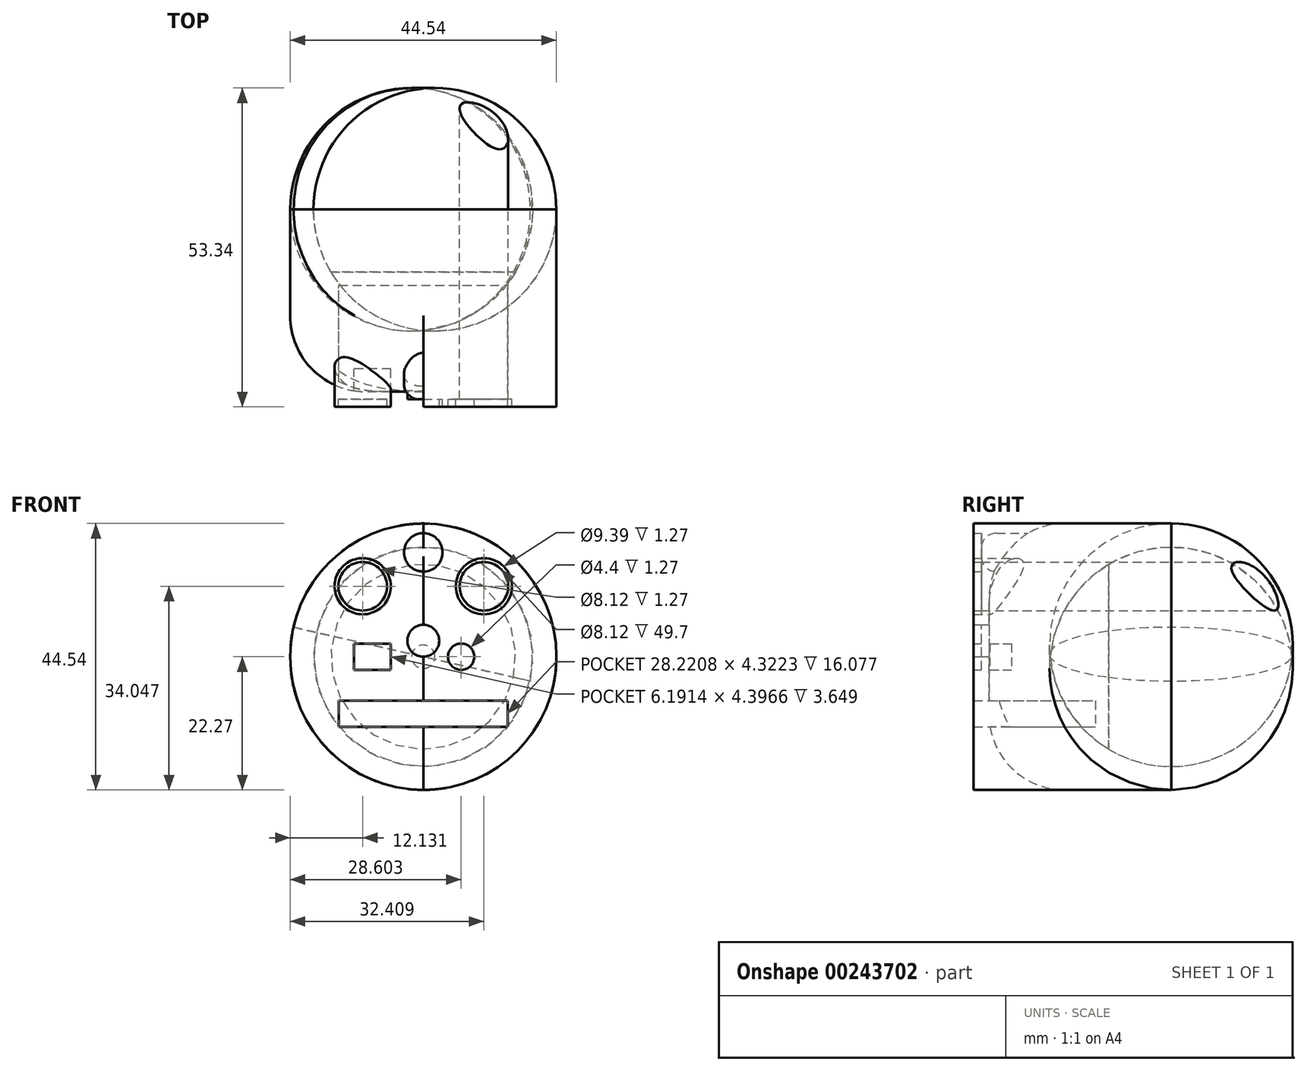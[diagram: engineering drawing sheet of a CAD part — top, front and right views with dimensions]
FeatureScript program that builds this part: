
annotation { "Feature Type Name" : "Feature", "Feature Type Description" : "" }
export const myFeature = defineFeature(function(context is Context, id is Id, definition is map)
    precondition{}
    {
        {
            var Q0;
            Q0=qCreatedBy(makeId("Front.planeOp"),FACE);
            var sketch = newSketch(context, id + "F0", { "sketchPlane" : qUnion([Q0])});
            skCircle(sketch, "E0", {"center": v(0, 0) * mm, "radius": 22.27 * mm});
            skLineSegment(sketch, "E1", {"start": v(0, 22.27) * mm, "end": v(0, -22.27) * mm});
            skCircle(sketch, "E2", {"center": v(-10.14, 11.78) * mm, "radius": 4.7 * mm});
            skLineSegment(sketch, "E3.bottom", {"start": v(-14.11, -7.38) * mm, "end": v(14.11, -7.38) * mm});
            skLineSegment(sketch, "E3.top", {"start": v(-14.11, -11.7) * mm, "end": v(14.11, -11.7) * mm});
            skLineSegment(sketch, "E3.left", {"start": v(-14.11, -7.38) * mm, "end": v(-14.11, -11.7) * mm});
            skLineSegment(sketch, "E3.right", {"start": v(14.11, -7.38) * mm, "end": v(14.11, -11.7) * mm});
            skPoint(sketch, "E3.middle", {"position": v(0, -9.54) * mm});
            skCircle(sketch, "E4", {"center": v(0, 2.67) * mm, "radius": 2.67 * mm});
            skCircle(sketch, "E5", {"center": v(0, 17.44) * mm, "radius": 3.22 * mm});
            skCircle(sketch, "E6.MirrorC", {"center": v(10.14, 11.78) * mm, "radius": 4.7 * mm});
            skLineSegment(sketch, "E7.bottom", {"start": v(-5.4, 2.2) * mm, "end": v(-11.6, 2.2) * mm});
            skLineSegment(sketch, "E7.top", {"start": v(-5.4, -2.2) * mm, "end": v(-11.6, -2.2) * mm});
            skLineSegment(sketch, "E7.left", {"start": v(-5.4, 2.2) * mm, "end": v(-5.4, -2.2) * mm});
            skLineSegment(sketch, "E7.right", {"start": v(-11.6, 2.2) * mm, "end": v(-11.6, -2.2) * mm});
            skPoint(sketch, "E7.middle", {"position": v(-8.5, 0) * mm});
            skCircle(sketch, "E8", {"center": v(6.33, 0) * mm, "radius": 2.2 * mm});
            skCircle(sketch, "E9", {"center": v(-10.14, 11.78) * mm, "radius": 4.06 * mm});
            skCircle(sketch, "E10.MirrorC", {"center": v(10.14, 11.78) * mm, "radius": 4.06 * mm});
            skSolve(sketch);
        }
        {
            var Q0;
            Q0=makeQuery(id+"F0.imprint","IMPRINT",FACE,{"disambiguationData":[TD([[makeQuery(id+"F0.imprint","IMPRINT",EDGE,{"derivedFrom":sQuery(id+"F0.wireOp",EDGE,"E2")}),-1.0]])]});
            var Q1;
            {var subQ4=sQuery(id+"F0.wireOp",EDGE,"E3.right");Q1=makeQuery(id+"F0.imprint","IMPRINT",FACE,{"disambiguationData":[TD([[makeQuery(id+"F0.imprint","IMPRINT",EDGE,{"derivedFrom":subQ4}),1.0]])]});}
            extrude(context, id + "F1", {"entities" : qUnion([Q0, Q1]), "depth" : 38.1 * mm});
        }
        {
            var Q0;
            Q0=makeQuery(id+"F1.opExtrude","CAP_EDGE",EDGE,{"disambiguationData":[OSD([sQuery(id+"F0.wireOp",EDGE,"E0")])],"isStart":false});
            fillet(context, id + "F2", {"entities" : qUnion([Q0]), "radius" : 12.7 * mm, "tangentPropagation" : true, "allowEdgeOverflow" : false});
        }
        {
            var Q0;
            Q0=makeQuery(id+"F0.imprint","IMPRINT",FACE,{"disambiguationData":[TD([[makeQuery(id+"F0.imprint","IMPRINT",EDGE,{"derivedFrom":sQuery(id+"F0.wireOp",EDGE,"E2")}),1.0]])]});
            var Q1;
            Q1=makeQuery(id+"F0.imprint","IMPRINT",FACE,{"disambiguationData":[TD([[makeQuery(id+"F0.imprint","IMPRINT",EDGE,{"derivedFrom":sQuery(id+"F0.wireOp",EDGE,"E6.MirrorC")}),-1.0]])]});
            extrude(context, id + "F3", {"entities" : qUnion([Q0, Q1]), "operationType" : NewBodyOperationType.ADD, "depth" : 40.64 * mm});
        }
        {
            var Q0;
            {var subQ5=sQuery(id+"F0.wireOp",EDGE,"E3.right");Q0=makeQuery(id+"F0.imprint","IMPRINT",FACE,{"disambiguationData":[TD([[makeQuery(id+"F0.imprint","IMPRINT",EDGE,{"derivedFrom":subQ5}),-1.0]])]});}
            var Q1;
            {var subQ5=sQuery(id+"F0.wireOp",EDGE,"E3.left");Q1=makeQuery(id+"F0.imprint","IMPRINT",FACE,{"disambiguationData":[TD([[makeQuery(id+"F0.imprint","IMPRINT",EDGE,{"derivedFrom":subQ5}),1.0]])]});}
            extrude(context, id + "F4", {"entities" : qUnion([Q0, Q1]), "operationType" : NewBodyOperationType.ADD, "depth" : 20.32 * mm});
        }
        {
            var Q0;
            {var subQ0=sQuery(id+"F0.wireOp",EDGE,"E5");var subQ1=sQuery(id+"F0.wireOp",EDGE,"E1");var subQ2=makeQuery(id+"F0.imprint","INTERSECT",VERTEX,{"disambiguationData":[OD(0.0)],"derivedFrom":[subQ1,subQ0]});Q0=makeQuery(id+"F0.imprint","IMPRINT",FACE,{"disambiguationData":[TD([[makeQuery(id+"F0.imprint","IMPRINT",EDGE,{"disambiguationData":[TD([[subQ2,-1.0]])],"derivedFrom":subQ1}),1.0]])]});}
            var Q1;
            {var subQ0=sQuery(id+"F0.wireOp",EDGE,"E5");var subQ1=sQuery(id+"F0.wireOp",EDGE,"E1");var subQ2=makeQuery(id+"F0.imprint","INTERSECT",VERTEX,{"disambiguationData":[OD(0.0)],"derivedFrom":[subQ1,subQ0]});Q1=makeQuery(id+"F0.imprint","IMPRINT",FACE,{"disambiguationData":[TD([[makeQuery(id+"F0.imprint","IMPRINT",EDGE,{"disambiguationData":[TD([[subQ2,-1.0]])],"derivedFrom":subQ1}),-1.0]])]});}
            extrude(context, id + "F5", {"entities" : qUnion([Q0, Q1]), "operationType" : NewBodyOperationType.ADD, "depth" : 39.37 * mm});
        }
        {
            var Q0;
            {var subQ0=sQuery(id+"F0.wireOp",EDGE,"E4");var subQ1=sQuery(id+"F0.wireOp",EDGE,"E1");var subQ2=makeQuery(id+"F0.imprint","INTERSECT",VERTEX,{"disambiguationData":[OD(0.0)],"derivedFrom":[subQ1,subQ0]});Q0=makeQuery(id+"F0.imprint","IMPRINT",FACE,{"disambiguationData":[TD([[makeQuery(id+"F0.imprint","IMPRINT",EDGE,{"disambiguationData":[TD([[subQ2,-1.0]])],"derivedFrom":subQ1}),-1.0]])]});}
            var Q1;
            {var subQ0=sQuery(id+"F0.wireOp",EDGE,"E4");var subQ1=sQuery(id+"F0.wireOp",EDGE,"E1");var subQ2=makeQuery(id+"F0.imprint","INTERSECT",VERTEX,{"disambiguationData":[OD(0.0)],"derivedFrom":[subQ1,subQ0]});Q1=makeQuery(id+"F0.imprint","IMPRINT",FACE,{"disambiguationData":[TD([[makeQuery(id+"F0.imprint","IMPRINT",EDGE,{"disambiguationData":[TD([[subQ2,-1.0]])],"derivedFrom":subQ1}),1.0]])]});}
            var Q2;
            Q2=makeQuery(id+"F0.imprint","IMPRINT",FACE,{"disambiguationData":[TD([[makeQuery(id+"F0.imprint","IMPRINT",EDGE,{"derivedFrom":sQuery(id+"F0.wireOp",EDGE,"E8")}),1.0]])]});
            extrude(context, id + "F6", {"entities" : qUnion([Q0, Q1, Q2]), "operationType" : NewBodyOperationType.ADD, "depth" : 39.37 * mm});
        }
        {
            var Q0;
            Q0=makeQuery(id+"F0.imprint","IMPRINT",FACE,{"disambiguationData":[TD([[makeQuery(id+"F0.imprint","IMPRINT",EDGE,{"derivedFrom":sQuery(id+"F0.wireOp",EDGE,"E7.bottom")}),1.0]])]});
            extrude(context, id + "F7", {"entities" : qUnion([Q0]), "operationType" : NewBodyOperationType.ADD, "depth" : 34.3 * mm});
        }
        {
            var Q0;
            Q0=makeQuery(id+"F0.imprint","IMPRINT",FACE,{"disambiguationData":[TD([[makeQuery(id+"F0.imprint","IMPRINT",EDGE,{"derivedFrom":sQuery(id+"F0.wireOp",EDGE,"E9")}),1.0]])]});
            var Q1;
            Q1=makeQuery(id+"F0.imprint","IMPRINT",FACE,{"disambiguationData":[TD([[makeQuery(id+"F0.imprint","IMPRINT",EDGE,{"derivedFrom":sQuery(id+"F0.wireOp",EDGE,"E10.MirrorC")}),-1.0]])]});
            extrude(context, id + "F8", {"entities" : qUnion([Q0, Q1]), "operationType" : NewBodyOperationType.ADD, "depth" : 39.37 * mm});
        }
        {
            var Q0;
            {var subQ0=sQuery(id+"F0.wireOp",EDGE,"E10.MirrorC");var subQ1=sQuery(id+"F0.wireOp",EDGE,"E9");var subQ2=sQuery(id+"F0.wireOp",EDGE,"E7.right");var subQ3=sQuery(id+"F0.wireOp",EDGE,"E7.left");var subQ4=sQuery(id+"F0.wireOp",EDGE,"E7.top");var subQ5=sQuery(id+"F0.wireOp",EDGE,"E7.bottom");var subQ6=sQuery(id+"F0.wireOp",EDGE,"E8");var subQ7=sQuery(id+"F0.wireOp",EDGE,"E4");var subQ8=sQuery(id+"F0.wireOp",EDGE,"E5");var subQ9=sQuery(id+"F0.wireOp",EDGE,"E3.right");var subQ10=sQuery(id+"F0.wireOp",EDGE,"E3.left");var subQ11=sQuery(id+"F0.wireOp",EDGE,"E3.top");var subQ12=sQuery(id+"F0.wireOp",EDGE,"E3.bottom");var subQ13=sQuery(id+"F0.wireOp",EDGE,"E6.MirrorC");var subQ14=sQuery(id+"F0.wireOp",EDGE,"E2");Q0=makeQuery(id+"F8.boolean.opBoolean","MERGE",FACE,{"derivedFrom":[makeQuery(id+"F7.boolean.opBoolean","MERGE",FACE,{"derivedFrom":[makeQuery(id+"F6.boolean.opBoolean","MERGE",FACE,{"derivedFrom":[makeQuery(id+"F5.boolean.opBoolean","MERGE",FACE,{"derivedFrom":[makeQuery(id+"F4.boolean.opBoolean","MERGE",FACE,{"derivedFrom":[makeQuery(id+"F3.boolean.opBoolean","MERGE",FACE,{"derivedFrom":[makeQuery(id+"F1.opExtrude","CAP_FACE",FACE,{"disambiguationData":[OSD([sQuery(id+"F0.wireOp",EDGE,"E0"),subQ14,subQ12,subQ11,subQ10,subQ9,subQ7,subQ8,subQ13,subQ5,subQ4,subQ3,subQ2,subQ6])],"isStart":true}),makeQuery(id+"F3.opExtrude","CAP_FACE",FACE,{"disambiguationData":[OSD([subQ14,subQ1])],"isStart":true}),makeQuery(id+"F3.opExtrude","CAP_FACE",FACE,{"disambiguationData":[OSD([subQ13,subQ0])],"isStart":true})]}),makeQuery(id+"F4.opExtrude","CAP_FACE",FACE,{"disambiguationData":[OSD([subQ12,subQ11,subQ10,subQ9])],"isStart":true})]}),makeQuery(id+"F5.opExtrude","CAP_FACE",FACE,{"disambiguationData":[OSD([subQ8])],"isStart":true})]}),makeQuery(id+"F6.opExtrude","CAP_FACE",FACE,{"disambiguationData":[OSD([subQ7])],"isStart":true}),makeQuery(id+"F6.opExtrude","CAP_FACE",FACE,{"disambiguationData":[OSD([subQ6])],"isStart":true})]}),makeQuery(id+"F7.opExtrude","CAP_FACE",FACE,{"disambiguationData":[OSD([subQ5,subQ4,subQ3,subQ2])],"isStart":true})]}),makeQuery(id+"F8.opExtrude","CAP_FACE",FACE,{"disambiguationData":[OSD([subQ1])],"isStart":true}),makeQuery(id+"F8.opExtrude","CAP_FACE",FACE,{"disambiguationData":[OSD([subQ0])],"isStart":true})]});}
            extrude(context, id + "F9", {"entities" : qUnion([Q0]), "operationType" : NewBodyOperationType.ADD, "depth" : 12.7 * mm});
        }
        {
            var Q0;
            Q0=makeQuery(id+"F9.opExtrude","CAP_EDGE",EDGE,{"disambiguationData":[OSD([sQuery(id+"F0.wireOp",EDGE,"E0")])],"isStart":false});
            fillet(context, id + "F10", {"entities" : qUnion([Q0]), "radius" : 20.32 * mm, "tangentPropagation" : true, "allowEdgeOverflow" : false});
        }
        {
            var Q0;
            Q0=makeQuery(id+"F5.opExtrude","CAP_EDGE",EDGE,{"disambiguationData":[OSD([sQuery(id+"F0.wireOp",EDGE,"E5")])],"isStart":false});
            fillet(context, id + "F11", {"entities" : qUnion([Q0]), "radius" : 2.54 * mm, "tangentPropagation" : true, "allowEdgeOverflow" : false});
        }
    });
